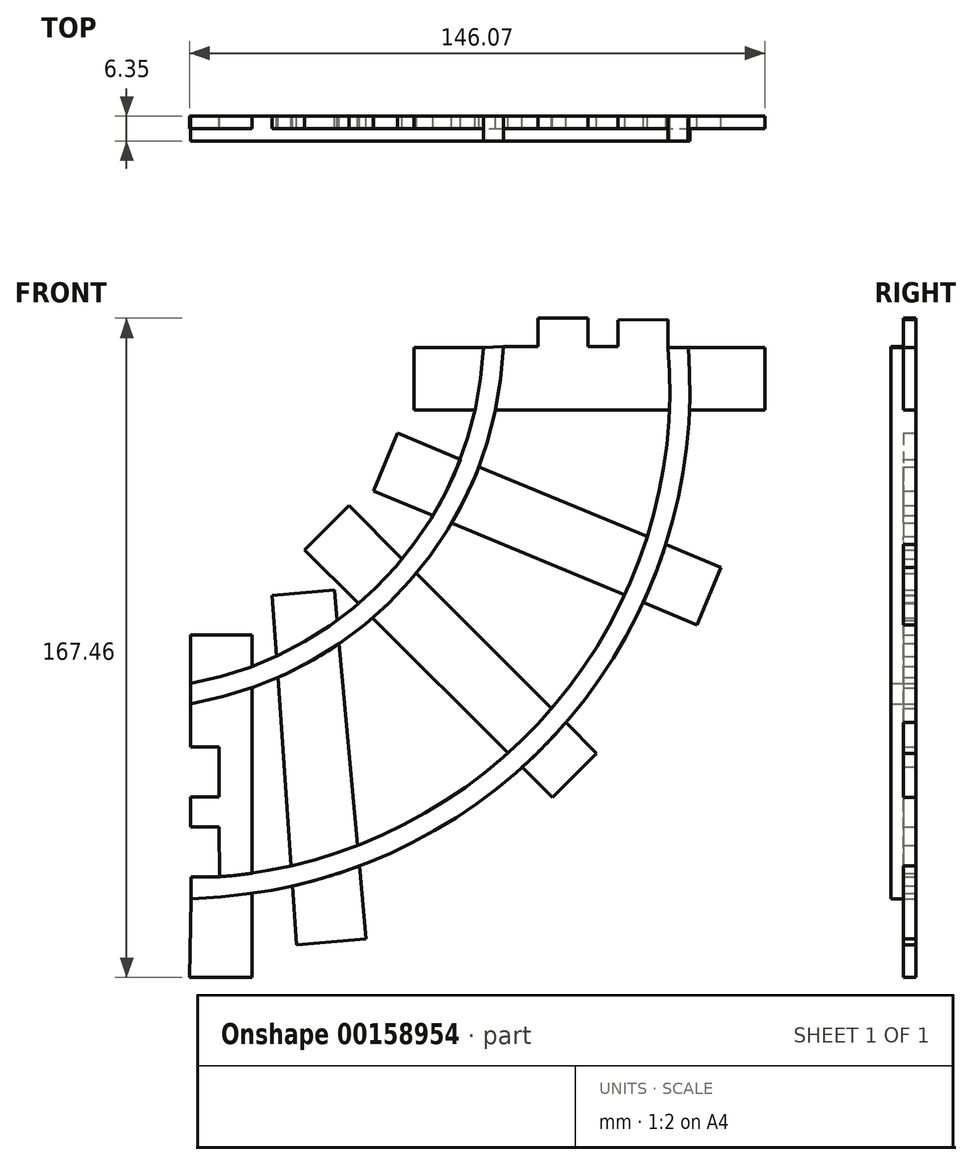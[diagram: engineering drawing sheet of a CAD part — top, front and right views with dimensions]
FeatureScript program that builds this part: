
annotation { "Feature Type Name" : "Feature", "Feature Type Description" : "" }
export const myFeature = defineFeature(function(context is Context, id is Id, definition is map)
    precondition{}
    {
        {
            var Q0;
            Q0=qCreatedBy(makeId("Front.planeOp"),FACE);
            var sketch = newSketch(context, id + "F0", { "sketchPlane" : qUnion([Q0])});
            skArc(sketch, "E0", {"start": v(0, -85.32) * mm, "mid": v(52.1, -55.65) * mm, "end": v(74.36, 0) * mm});
            skArc(sketch, "E1.0", {"start": v(0, -90.48) * mm, "mid": v(55.76, -59.17) * mm, "end": v(79.46, 0.22) * mm});
            skLineSegment(sketch, "E2.top", {"start": v(56.79, -15.84) * mm, "end": v(145.82, -15.84) * mm});
            skLineSegment(sketch, "E2.left", {"start": v(56.79, 0) * mm, "end": v(56.79, -15.84) * mm});
            skLineSegment(sketch, "E2.right", {"start": v(145.82, 0) * mm, "end": v(145.82, -15.84) * mm});
            skLineSegment(sketch, "E3", {"start": v(108.5, 0.22) * mm, "end": v(108.5, 7) * mm});
            skLineSegment(sketch, "E4", {"start": v(121.2, 7.19) * mm, "end": v(121.3, 0) * mm});
            skLineSegment(sketch, "E5.bottom", {"start": v(88.19, 0.27) * mm, "end": v(100.89, 0.27) * mm});
            skLineSegment(sketch, "E5.top", {"start": v(88.19, 7.47) * mm, "end": v(100.89, 7.47) * mm});
            skLineSegment(sketch, "E5.left", {"start": v(88.19, 0.27) * mm, "end": v(88.19, 7.47) * mm});
            skLineSegment(sketch, "E5.right", {"start": v(100.89, 0.27) * mm, "end": v(100.89, 7.47) * mm});
            skLineSegment(sketch, "E6", {"start": v(108.5, 7) * mm, "end": v(121.2, 7.19) * mm});
            skLineSegment(sketch, "E7.bottom", {"start": v(0, -72.94) * mm, "end": v(15.54, -72.94) * mm});
            skLineSegment(sketch, "E7.top", {"start": v(-0.25, -159.99) * mm, "end": v(15.54, -159.99) * mm});
            skLineSegment(sketch, "E7.right", {"start": v(15.54, -72.94) * mm, "end": v(15.54, -159.99) * mm});
            skLineSegment(sketch, "E8.bottom", {"start": v(0, -121.74) * mm, "end": v(7.19, -121.74) * mm});
            skLineSegment(sketch, "E8.top", {"start": v(0.11, -134.44) * mm, "end": v(7.35, -134.44) * mm});
            skLineSegment(sketch, "E8.right", {"start": v(7.19, -121.74) * mm, "end": v(7.3, -134.46) * mm});
            skLineSegment(sketch, "E9.bottom", {"start": v(0, -101.42) * mm, "end": v(7.19, -101.42) * mm});
            skLineSegment(sketch, "E9.top", {"start": v(0, -114.12) * mm, "end": v(7.19, -114.12) * mm});
            skLineSegment(sketch, "E9.right", {"start": v(7.19, -101.42) * mm, "end": v(7.19, -114.12) * mm});
            skLineSegment(sketch, "E10", {"start": v(0, -72.94) * mm, "end": v(0, -101.42) * mm});
            skLineSegment(sketch, "E11", {"start": v(0.11, -134.44) * mm, "end": v(-0.25, -159.99) * mm});
            skLineSegment(sketch, "E12", {"start": v(0, -114.12) * mm, "end": v(0, -121.74) * mm});
            skLineSegment(sketch, "E13", {"start": v(20.7, -62.96) * mm, "end": v(36.48, -61.53) * mm});
            skLineSegment(sketch, "E14", {"start": v(36.48, -61.53) * mm, "end": v(44.52, -150.17) * mm});
            skLineSegment(sketch, "E15", {"start": v(44.52, -150.17) * mm, "end": v(26.9, -151.77) * mm});
            skLineSegment(sketch, "E16", {"start": v(26.9, -151.77) * mm, "end": v(20.7, -62.96) * mm});
            skLineSegment(sketch, "E17.1.0", {"start": v(52.47, -21.73) * mm, "end": v(134.72, -55.8) * mm});
            skLineSegment(sketch, "E17.1.1", {"start": v(52.47, -21.73) * mm, "end": v(46.4, -36.36) * mm});
            skLineSegment(sketch, "E17.1.2", {"start": v(46.4, -36.36) * mm, "end": v(128.66, -70.43) * mm});
            skLineSegment(sketch, "E17.1.3", {"start": v(134.72, -55.8) * mm, "end": v(128.66, -70.43) * mm});
            skLineSegment(sketch, "E17.2.0", {"start": v(40.16, -40.16) * mm, "end": v(103.1, -103.1) * mm});
            skLineSegment(sketch, "E17.2.1", {"start": v(40.16, -40.16) * mm, "end": v(28.96, -51.36) * mm});
            skLineSegment(sketch, "E17.2.2", {"start": v(28.96, -51.36) * mm, "end": v(91.91, -114.3) * mm});
            skLineSegment(sketch, "E17.2.3", {"start": v(103.1, -103.1) * mm, "end": v(91.91, -114.3) * mm});
            skPoint(sketch, "E17.center", {"position": v(0, 0) * mm});
            skLineSegment(sketch, "E17.anchor1", {"start": v(0, 0) * mm, "end": v(56.79, 0) * mm, "construction": true});
            skLineSegment(sketch, "E17.anchor2", {"start": v(0, 0) * mm, "end": v(40.16, -40.16) * mm, "construction": true});
            skLineSegment(sketch, "E18", {"start": v(56.79, 0) * mm, "end": v(74.36, 0) * mm});
            skLineSegment(sketch, "E19", {"start": v(79.46, 0.22) * mm, "end": v(74.36, 0) * mm});
            skLineSegment(sketch, "E20", {"start": v(88.19, 0.27) * mm, "end": v(79.46, 0.22) * mm});
            skLineSegment(sketch, "E21", {"start": v(108.5, 0.22) * mm, "end": v(100.89, 0.27) * mm});
            skLineSegment(sketch, "E22", {"start": v(121.3, 0) * mm, "end": v(126.38, 0.07) * mm});
            skLineSegment(sketch, "E23", {"start": v(145.82, 0) * mm, "end": v(126.38, 0.07) * mm});
            skLineSegment(sketch, "E24", {"start": v(108.5, 0.22) * mm, "end": v(121.3, 0) * mm});
            skArc(sketch, "E25", {"start": v(7.35, -134.44) * mm, "mid": v(92.3, -90.93) * mm, "end": v(121.3, 0) * mm});
            skArc(sketch, "E26.0", {"start": v(7.75, -139.5) * mm, "mid": v(96.17, -94.21) * mm, "end": v(126.36, 0.43) * mm});
            skLineSegment(sketch, "E27", {"start": v(7.75, -139.5) * mm, "end": v(0.03, -140.11) * mm});
            skSolve(sketch);
        }
        {
            var Q0;
            {var subQ5=sQuery(id+"F0.wireOp",EDGE,"E7.bottom");Q0=makeQuery(id+"F0.imprint","IMPRINT",FACE,{"disambiguationData":[TD([[makeQuery(id+"F0.imprint","IMPRINT",EDGE,{"derivedFrom":subQ5}),-1.0]])]});}
            var Q1;
            {var subQ5=sQuery(id+"F0.wireOp",EDGE,"E7.top");Q1=makeQuery(id+"F0.imprint","IMPRINT",FACE,{"disambiguationData":[TD([[makeQuery(id+"F0.imprint","IMPRINT",EDGE,{"derivedFrom":subQ5}),1.0]])]});}
            var Q2;
            {var subQ0=sQuery(id+"F0.wireOp",EDGE,"E16");var subQ1=sQuery(id+"F0.wireOp",EDGE,"XXZ0oDVb-x05m-eHWM-CYOe-lrHYANyUXMwL");var subQ2=makeQuery(id+"F0.imprint","INTERSECT",VERTEX,{"derivedFrom":[subQ1,subQ0]});Q2=makeQuery(id+"F0.imprint","IMPRINT",FACE,{"disambiguationData":[TD([[makeQuery(id+"F0.imprint","IMPRINT",EDGE,{"disambiguationData":[TD([[subQ2,-1.0]])],"derivedFrom":subQ1}),1.0]])]});}
            var Q3;
            {var subQ5=sQuery(id+"F0.wireOp",EDGE,"E15");Q3=makeQuery(id+"F0.imprint","IMPRINT",FACE,{"disambiguationData":[TD([[makeQuery(id+"F0.imprint","IMPRINT",EDGE,{"derivedFrom":subQ5}),-1.0]])]});}
            var Q4;
            {var subQ5=sQuery(id+"F0.wireOp",EDGE,"E13");Q4=makeQuery(id+"F0.imprint","IMPRINT",FACE,{"disambiguationData":[TD([[makeQuery(id+"F0.imprint","IMPRINT",EDGE,{"derivedFrom":subQ5}),-1.0]])]});}
            var Q5;
            {var subQ5=sQuery(id+"F0.wireOp",EDGE,"E17.2.1");Q5=makeQuery(id+"F0.imprint","IMPRINT",FACE,{"disambiguationData":[TD([[makeQuery(id+"F0.imprint","IMPRINT",EDGE,{"derivedFrom":subQ5}),1.0]])]});}
            var Q6;
            {var subQ0=sQuery(id+"F0.wireOp",EDGE,"E17.2.2");var subQ1=sQuery(id+"F0.wireOp",EDGE,"XXZ0oDVb-x05m-eHWM-CYOe-lrHYANyUXMwL");var subQ2=makeQuery(id+"F0.imprint","INTERSECT",VERTEX,{"derivedFrom":[subQ1,subQ0]});Q6=makeQuery(id+"F0.imprint","IMPRINT",FACE,{"disambiguationData":[TD([[makeQuery(id+"F0.imprint","IMPRINT",EDGE,{"disambiguationData":[TD([[subQ2,-1.0]])],"derivedFrom":subQ1}),1.0]])]});}
            var Q7;
            {var subQ5=sQuery(id+"F0.wireOp",EDGE,"E17.2.3");Q7=makeQuery(id+"F0.imprint","IMPRINT",FACE,{"disambiguationData":[TD([[makeQuery(id+"F0.imprint","IMPRINT",EDGE,{"derivedFrom":subQ5}),-1.0]])]});}
            var Q8;
            {var subQ5=sQuery(id+"F0.wireOp",EDGE,"E17.1.3");Q8=makeQuery(id+"F0.imprint","IMPRINT",FACE,{"disambiguationData":[TD([[makeQuery(id+"F0.imprint","IMPRINT",EDGE,{"derivedFrom":subQ5}),-1.0]])]});}
            var Q9;
            {var subQ0=sQuery(id+"F0.wireOp",EDGE,"E17.1.2");var subQ1=sQuery(id+"F0.wireOp",EDGE,"XXZ0oDVb-x05m-eHWM-CYOe-lrHYANyUXMwL");var subQ2=makeQuery(id+"F0.imprint","INTERSECT",VERTEX,{"derivedFrom":[subQ1,subQ0]});Q9=makeQuery(id+"F0.imprint","IMPRINT",FACE,{"disambiguationData":[TD([[makeQuery(id+"F0.imprint","IMPRINT",EDGE,{"disambiguationData":[TD([[subQ2,-1.0]])],"derivedFrom":subQ1}),1.0]])]});}
            var Q10;
            {var subQ5=sQuery(id+"F0.wireOp",EDGE,"E17.1.1");Q10=makeQuery(id+"F0.imprint","IMPRINT",FACE,{"disambiguationData":[TD([[makeQuery(id+"F0.imprint","IMPRINT",EDGE,{"derivedFrom":subQ5}),1.0]])]});}
            var Q11;
            {var subQ5=sQuery(id+"F0.wireOp",EDGE,"E2.left");Q11=makeQuery(id+"F0.imprint","IMPRINT",FACE,{"disambiguationData":[TD([[makeQuery(id+"F0.imprint","IMPRINT",EDGE,{"derivedFrom":subQ5}),1.0]])]});}
            var Q12;
            {var subQ0=sQuery(id+"F0.wireOp",EDGE,"E2.bottom");var subQ7=sQuery(id+"F0.wireOp",EDGE,"XXZ0oDVb-x05m-eHWM-CYOe-lrHYANyUXMwL");var subQ9=makeQuery(id+"F0.imprint","INTERSECT",VERTEX,{"derivedFrom":[subQ7,subQ0]});Q12=makeQuery(id+"F0.imprint","IMPRINT",FACE,{"disambiguationData":[TD([[makeQuery(id+"F0.imprint","IMPRINT",EDGE,{"disambiguationData":[TD([[subQ9,1.0]])],"derivedFrom":subQ7}),1.0]])]});}
            var Q13;
            {var subQ0=sQuery(id+"F0.wireOp",EDGE,"E2.right");Q13=makeQuery(id+"F0.imprint","IMPRINT",FACE,{"disambiguationData":[TD([[makeQuery(id+"F0.imprint","IMPRINT",EDGE,{"derivedFrom":subQ0}),-1.0]])]});}
            var Q14;
            Q14=makeQuery(id+"F0.imprint","IMPRINT",FACE,{"disambiguationData":[TD([[makeQuery(id+"F0.imprint","IMPRINT",EDGE,{"derivedFrom":sQuery(id+"F0.wireOp",EDGE,"E5.bottom")}),1.0]])]});
            var Q15;
            {var subQ0=sQuery(id+"F0.wireOp",EDGE,"E3");Q15=makeQuery(id+"F0.imprint","IMPRINT",FACE,{"disambiguationData":[TD([[makeQuery(id+"F0.imprint","IMPRINT",EDGE,{"derivedFrom":subQ0}),-1.0]])]});}
            var Q16;
            {var subQ7=sQuery(id+"F0.wireOp",EDGE,"E8.bottom");Q16=makeQuery(id+"F0.imprint","IMPRINT",FACE,{"disambiguationData":[TD([[makeQuery(id+"F0.imprint","IMPRINT",EDGE,{"derivedFrom":subQ7}),1.0]])]});}
            var Q17;
            Q17=makeQuery(id+"F0.imprint","IMPRINT",FACE,{"disambiguationData":[TD([[makeQuery(id+"F0.imprint","IMPRINT",EDGE,{"derivedFrom":sQuery(id+"F0.wireOp",EDGE,"E5.bottom")}),-1.0]])]});
            var Q18;
            {var subQ0=sQuery(id+"F0.wireOp",EDGE,"E17.1.2");var subQ1=sQuery(id+"F0.wireOp",EDGE,"E1.0");var subQ2=makeQuery(id+"F0.imprint","INTERSECT",VERTEX,{"derivedFrom":[subQ1,subQ0]});Q18=makeQuery(id+"F0.imprint","IMPRINT",FACE,{"disambiguationData":[TD([[makeQuery(id+"F0.imprint","IMPRINT",EDGE,{"disambiguationData":[TD([[subQ2,-1.0]])],"derivedFrom":subQ1}),-1.0]])]});}
            var Q19;
            {var subQ0=sQuery(id+"F0.wireOp",EDGE,"E17.2.2");var subQ1=sQuery(id+"F0.wireOp",EDGE,"E1.0");var subQ2=makeQuery(id+"F0.imprint","INTERSECT",VERTEX,{"derivedFrom":[subQ1,subQ0]});Q19=makeQuery(id+"F0.imprint","IMPRINT",FACE,{"disambiguationData":[TD([[makeQuery(id+"F0.imprint","IMPRINT",EDGE,{"disambiguationData":[TD([[subQ2,-1.0]])],"derivedFrom":subQ1}),-1.0]])]});}
            var Q20;
            {var subQ0=sQuery(id+"F0.wireOp",EDGE,"E16");var subQ1=sQuery(id+"F0.wireOp",EDGE,"E1.0");var subQ2=makeQuery(id+"F0.imprint","INTERSECT",VERTEX,{"derivedFrom":[subQ1,subQ0]});Q20=makeQuery(id+"F0.imprint","IMPRINT",FACE,{"disambiguationData":[TD([[makeQuery(id+"F0.imprint","IMPRINT",EDGE,{"disambiguationData":[TD([[subQ2,-1.0]])],"derivedFrom":subQ1}),-1.0]])]});}
            extrude(context, id + "F1", {"entities" : qUnion([Q0, Q1, Q2, Q3, Q4, Q5, Q6, Q7, Q8, Q9, Q10, Q11, Q12, Q13, Q14, Q15, Q16, Q17, Q18, Q19, Q20]), "depth" : 3.17 * mm});
        }
        {
            var Q0;
            {var subQ0=sQuery(id+"F0.wireOp",EDGE,"E19");Q0=makeQuery(id+"F0.imprint","IMPRINT",FACE,{"disambiguationData":[TD([[makeQuery(id+"F0.imprint","IMPRINT",EDGE,{"derivedFrom":subQ0}),1.0]])]});}
            var Q1;
            {var subQ0=sQuery(id+"F0.wireOp",EDGE,"E17.1.0");var subQ1=sQuery(id+"F0.wireOp",EDGE,"E0");var subQ2=makeQuery(id+"F0.imprint","INTERSECT",VERTEX,{"derivedFrom":[subQ1,subQ0]});Q1=makeQuery(id+"F0.imprint","IMPRINT",FACE,{"disambiguationData":[TD([[makeQuery(id+"F0.imprint","IMPRINT",EDGE,{"disambiguationData":[TD([[subQ2,-1.0]])],"derivedFrom":subQ1}),-1.0]])]});}
            var Q2;
            {var subQ0=sQuery(id+"F0.wireOp",EDGE,"E17.1.2");var subQ1=sQuery(id+"F0.wireOp",EDGE,"E0");var subQ2=makeQuery(id+"F0.imprint","INTERSECT",VERTEX,{"derivedFrom":[subQ1,subQ0]});Q2=makeQuery(id+"F0.imprint","IMPRINT",FACE,{"disambiguationData":[TD([[makeQuery(id+"F0.imprint","IMPRINT",EDGE,{"disambiguationData":[TD([[subQ2,-1.0]])],"derivedFrom":subQ1}),-1.0]])]});}
            var Q3;
            {var subQ0=sQuery(id+"F0.wireOp",EDGE,"E17.2.0");var subQ1=sQuery(id+"F0.wireOp",EDGE,"E0");var subQ2=makeQuery(id+"F0.imprint","INTERSECT",VERTEX,{"derivedFrom":[subQ1,subQ0]});Q3=makeQuery(id+"F0.imprint","IMPRINT",FACE,{"disambiguationData":[TD([[makeQuery(id+"F0.imprint","IMPRINT",EDGE,{"disambiguationData":[TD([[subQ2,-1.0]])],"derivedFrom":subQ1}),-1.0]])]});}
            var Q4;
            {var subQ0=sQuery(id+"F0.wireOp",EDGE,"E17.2.2");var subQ1=sQuery(id+"F0.wireOp",EDGE,"E0");var subQ2=makeQuery(id+"F0.imprint","INTERSECT",VERTEX,{"derivedFrom":[subQ1,subQ0]});Q4=makeQuery(id+"F0.imprint","IMPRINT",FACE,{"disambiguationData":[TD([[makeQuery(id+"F0.imprint","IMPRINT",EDGE,{"disambiguationData":[TD([[subQ2,-1.0]])],"derivedFrom":subQ1}),-1.0]])]});}
            var Q5;
            {var subQ0=sQuery(id+"F0.wireOp",EDGE,"E14");var subQ1=sQuery(id+"F0.wireOp",EDGE,"E0");var subQ2=makeQuery(id+"F0.imprint","INTERSECT",VERTEX,{"derivedFrom":[subQ1,subQ0]});Q5=makeQuery(id+"F0.imprint","IMPRINT",FACE,{"disambiguationData":[TD([[makeQuery(id+"F0.imprint","IMPRINT",EDGE,{"disambiguationData":[TD([[subQ2,-1.0]])],"derivedFrom":subQ1}),-1.0]])]});}
            var Q6;
            {var subQ0=sQuery(id+"F0.wireOp",EDGE,"E16");var subQ1=sQuery(id+"F0.wireOp",EDGE,"E0");var subQ2=makeQuery(id+"F0.imprint","INTERSECT",VERTEX,{"derivedFrom":[subQ1,subQ0]});Q6=makeQuery(id+"F0.imprint","IMPRINT",FACE,{"disambiguationData":[TD([[makeQuery(id+"F0.imprint","IMPRINT",EDGE,{"disambiguationData":[TD([[subQ2,-1.0]])],"derivedFrom":subQ1}),-1.0]])]});}
            var Q7;
            {var subQ0=sQuery(id+"F0.wireOp",EDGE,"E7.right");var subQ1=sQuery(id+"F0.wireOp",EDGE,"E0");var subQ2=makeQuery(id+"F0.imprint","INTERSECT",VERTEX,{"derivedFrom":[subQ1,subQ0]});Q7=makeQuery(id+"F0.imprint","IMPRINT",FACE,{"disambiguationData":[TD([[makeQuery(id+"F0.imprint","IMPRINT",EDGE,{"disambiguationData":[TD([[subQ2,-1.0]])],"derivedFrom":subQ1}),-1.0]])]});}
            var Q8;
            {var subQ0=sQuery(id+"F0.wireOp",EDGE,"E10");var subQ1=sQuery(id+"F0.wireOp",EDGE,"E0");var subQ2=makeQuery(id+"F0.imprint","INTERSECT",VERTEX,{"derivedFrom":[subQ1,subQ0]});Q8=makeQuery(id+"F0.imprint","IMPRINT",FACE,{"disambiguationData":[TD([[makeQuery(id+"F0.imprint","IMPRINT",EDGE,{"disambiguationData":[TD([[subQ2,-1.0]])],"derivedFrom":subQ1}),-1.0]])]});}
            var Q9;
            {var subQ6=sQuery(id+"F0.wireOp",EDGE,"E27");Q9=makeQuery(id+"F0.imprint","IMPRINT",FACE,{"disambiguationData":[TD([[makeQuery(id+"F0.imprint","IMPRINT",EDGE,{"derivedFrom":subQ6}),-1.0]])]});}
            var Q10;
            {var subQ0=sQuery(id+"F0.wireOp",EDGE,"E26.0");var subQ1=sQuery(id+"F0.wireOp",EDGE,"E7.right");var subQ2=makeQuery(id+"F0.imprint","INTERSECT",VERTEX,{"derivedFrom":[subQ1,subQ0]});Q10=makeQuery(id+"F0.imprint","IMPRINT",FACE,{"disambiguationData":[TD([[makeQuery(id+"F0.imprint","IMPRINT",EDGE,{"disambiguationData":[TD([[subQ2,1.0]])],"derivedFrom":subQ1}),1.0]])]});}
            var Q11;
            {var subQ0=sQuery(id+"F0.wireOp",EDGE,"E26.0");var subQ1=sQuery(id+"F0.wireOp",EDGE,"E14");var subQ2=makeQuery(id+"F0.imprint","INTERSECT",VERTEX,{"derivedFrom":[subQ1,subQ0]});Q11=makeQuery(id+"F0.imprint","IMPRINT",FACE,{"disambiguationData":[TD([[makeQuery(id+"F0.imprint","IMPRINT",EDGE,{"disambiguationData":[TD([[subQ2,1.0]])],"derivedFrom":subQ1}),-1.0]])]});}
            var Q12;
            {var subQ0=sQuery(id+"F0.wireOp",EDGE,"E26.0");var subQ1=sQuery(id+"F0.wireOp",EDGE,"E14");var subQ2=makeQuery(id+"F0.imprint","INTERSECT",VERTEX,{"derivedFrom":[subQ1,subQ0]});Q12=makeQuery(id+"F0.imprint","IMPRINT",FACE,{"disambiguationData":[TD([[makeQuery(id+"F0.imprint","IMPRINT",EDGE,{"disambiguationData":[TD([[subQ2,1.0]])],"derivedFrom":subQ1}),1.0]])]});}
            var Q13;
            {var subQ0=sQuery(id+"F0.wireOp",EDGE,"E26.0");var subQ1=sQuery(id+"F0.wireOp",EDGE,"E17.2.0");var subQ2=makeQuery(id+"F0.imprint","INTERSECT",VERTEX,{"derivedFrom":[subQ1,subQ0]});Q13=makeQuery(id+"F0.imprint","IMPRINT",FACE,{"disambiguationData":[TD([[makeQuery(id+"F0.imprint","IMPRINT",EDGE,{"disambiguationData":[TD([[subQ2,1.0]])],"derivedFrom":subQ1}),-1.0]])]});}
            var Q14;
            {var subQ0=sQuery(id+"F0.wireOp",EDGE,"E26.0");var subQ1=sQuery(id+"F0.wireOp",EDGE,"E17.1.2");var subQ2=makeQuery(id+"F0.imprint","INTERSECT",VERTEX,{"derivedFrom":[subQ1,subQ0]});Q14=makeQuery(id+"F0.imprint","IMPRINT",FACE,{"disambiguationData":[TD([[makeQuery(id+"F0.imprint","IMPRINT",EDGE,{"disambiguationData":[TD([[subQ2,1.0]])],"derivedFrom":subQ1}),-1.0]])]});}
            var Q15;
            {var subQ0=sQuery(id+"F0.wireOp",EDGE,"E26.0");var subQ1=sQuery(id+"F0.wireOp",EDGE,"E17.1.0");var subQ2=makeQuery(id+"F0.imprint","INTERSECT",VERTEX,{"derivedFrom":[subQ1,subQ0]});Q15=makeQuery(id+"F0.imprint","IMPRINT",FACE,{"disambiguationData":[TD([[makeQuery(id+"F0.imprint","IMPRINT",EDGE,{"disambiguationData":[TD([[subQ2,1.0]])],"derivedFrom":subQ1}),-1.0]])]});}
            var Q16;
            {var subQ0=sQuery(id+"F0.wireOp",EDGE,"E26.0");var subQ1=sQuery(id+"F0.wireOp",EDGE,"E2.top");var subQ2=makeQuery(id+"F0.imprint","INTERSECT",VERTEX,{"derivedFrom":[subQ1,subQ0]});Q16=makeQuery(id+"F0.imprint","IMPRINT",FACE,{"disambiguationData":[TD([[makeQuery(id+"F0.imprint","IMPRINT",EDGE,{"disambiguationData":[TD([[subQ2,1.0]])],"derivedFrom":subQ1}),-1.0]])]});}
            var Q17;
            {var subQ1=sQuery(id+"F0.wireOp",EDGE,"E22");Q17=makeQuery(id+"F0.imprint","IMPRINT",FACE,{"disambiguationData":[TD([[makeQuery(id+"F0.imprint","IMPRINT",EDGE,{"derivedFrom":subQ1}),-1.0]])]});}
            extrude(context, id + "F2", {"entities" : qUnion([Q0, Q1, Q2, Q3, Q4, Q5, Q6, Q7, Q8, Q9, Q10, Q11, Q12, Q13, Q14, Q15, Q16, Q17]), "depth" : 6.35 * mm});
        }
    });
